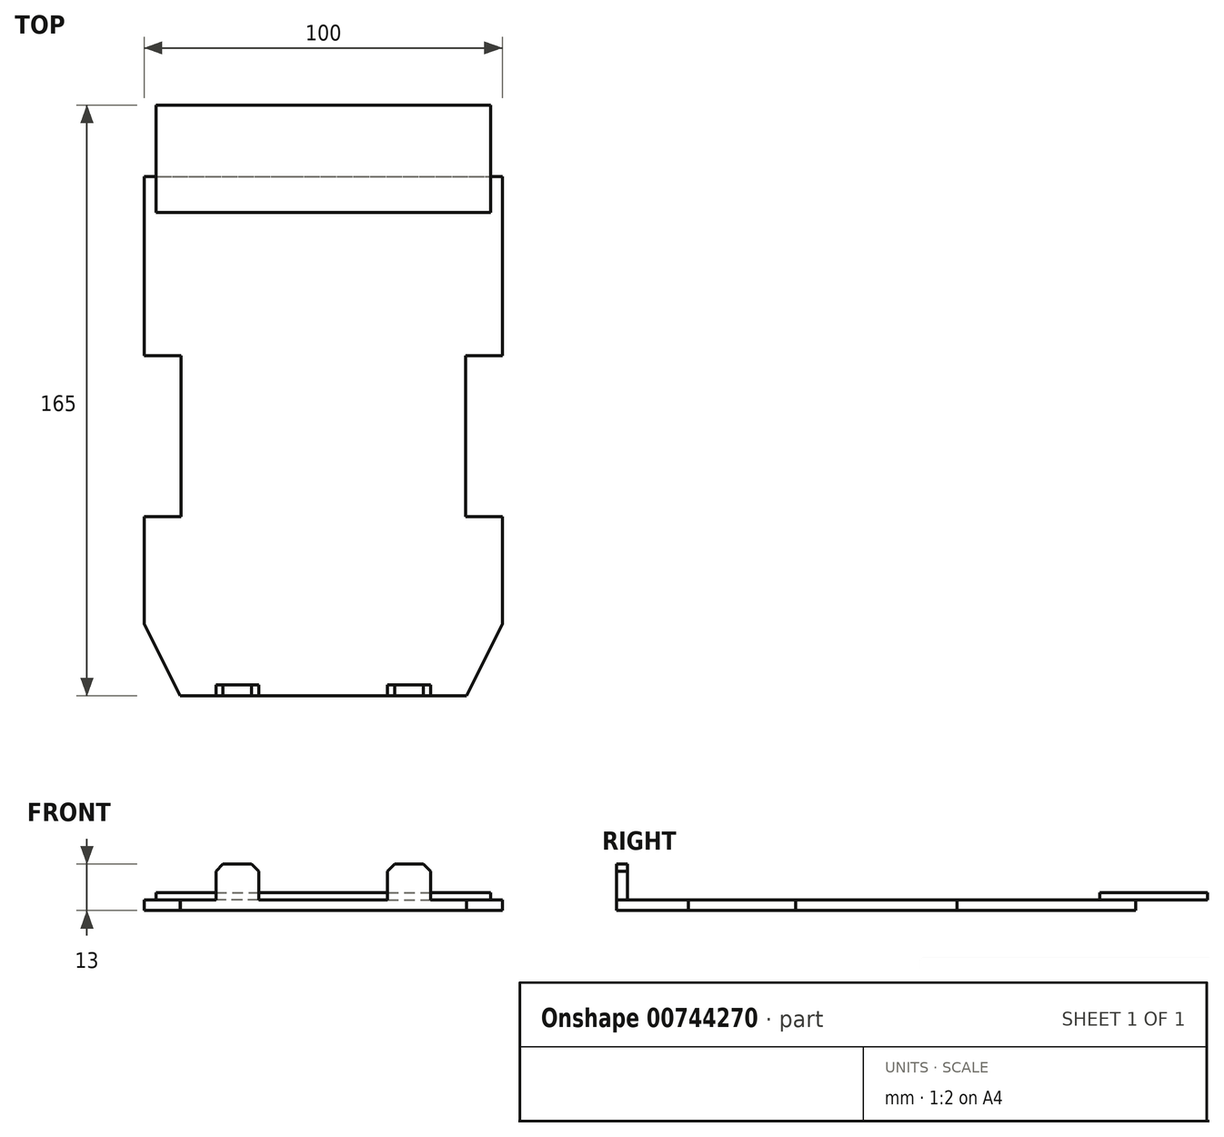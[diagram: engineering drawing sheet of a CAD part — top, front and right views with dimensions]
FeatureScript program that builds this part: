
annotation { "Feature Type Name" : "Feature", "Feature Type Description" : "" }
export const myFeature = defineFeature(function(context is Context, id is Id, definition is map)
    precondition{}
    {
        {
            var Q0;
            Q0=qCreatedBy(makeId("Top.planeOp"),FACE);
            var sketch = newSketch(context, id + "F0", { "sketchPlane" : qUnion([Q0])});
            skLineSegment(sketch, "E0", {"start": v(-30, 56.12) * mm, "end": v(30, 56.12) * mm});
            skLineSegment(sketch, "E1", {"start": v(30, 56.12) * mm, "end": v(50, 41.12) * mm});
            skLineSegment(sketch, "E2", {"start": v(-30, 56.12) * mm, "end": v(-50, 41.12) * mm});
            skLineSegment(sketch, "E3", {"start": v(-50, 41.12) * mm, "end": v(-50, 16.12) * mm});
            skLineSegment(sketch, "E4", {"start": v(-50, 16.12) * mm, "end": v(-42.8, 16.12) * mm});
            skLineSegment(sketch, "E5", {"start": v(-42.8, 16.12) * mm, "end": v(-42.8, -8.88) * mm});
            skLineSegment(sketch, "E6", {"start": v(-42.8, -8.88) * mm, "end": v(-50, -8.88) * mm});
            skLineSegment(sketch, "E7", {"start": v(-50, -8.88) * mm, "end": v(-50, -68.88) * mm});
            skLineSegment(sketch, "E8", {"start": v(-50, -68.88) * mm, "end": v(-39.78, -68.88) * mm});
            skLineSegment(sketch, "E9", {"start": v(-39.78, -68.88) * mm, "end": v(-39.78, -113.88) * mm});
            skLineSegment(sketch, "E10", {"start": v(-39.78, -113.88) * mm, "end": v(-50, -113.88) * mm});
            skLineSegment(sketch, "E11", {"start": v(-50, -113.88) * mm, "end": v(-50, -143.88) * mm});
            skLineSegment(sketch, "E12", {"start": v(-50, -143.88) * mm, "end": v(-40, -163.88) * mm});
            skLineSegment(sketch, "E13", {"start": v(-40, -163.88) * mm, "end": v(40, -163.88) * mm});
            skLineSegment(sketch, "E14.MirrorCS", {"start": v(50, 41.12) * mm, "end": v(50, 16.12) * mm});
            skLineSegment(sketch, "E15.MirrorCS", {"start": v(50, 16.12) * mm, "end": v(42.8, 16.12) * mm});
            skLineSegment(sketch, "E16.MirrorCS", {"start": v(42.8, 16.12) * mm, "end": v(42.8, -8.88) * mm});
            skLineSegment(sketch, "E17.MirrorCS", {"start": v(42.8, -8.88) * mm, "end": v(50, -8.88) * mm});
            skLineSegment(sketch, "E18.MirrorCS", {"start": v(50, -8.88) * mm, "end": v(50, -68.88) * mm});
            skLineSegment(sketch, "E19.MirrorCS", {"start": v(50, -68.88) * mm, "end": v(39.78, -68.88) * mm});
            skLineSegment(sketch, "E20.MirrorCS", {"start": v(39.78, -68.88) * mm, "end": v(39.78, -113.88) * mm});
            skLineSegment(sketch, "E21.MirrorCS", {"start": v(39.78, -113.88) * mm, "end": v(50, -113.88) * mm});
            skLineSegment(sketch, "E22.MirrorCS", {"start": v(50, -113.88) * mm, "end": v(50, -143.88) * mm});
            skLineSegment(sketch, "E23.MirrorCS", {"start": v(50, -143.88) * mm, "end": v(40, -163.88) * mm});
            skLineSegment(sketch, "E24", {"start": v(-50, -18.88) * mm, "end": v(50, -18.88) * mm});
            skSolve(sketch);
        }
        {
            var Q0;
            {var subQ0=sQuery(id+"F0.wireOp",EDGE,"E8");Q0=makeQuery(id+"F0.imprint","IMPRINT",FACE,{"disambiguationData":[TD([[makeQuery(id+"F0.imprint","IMPRINT",EDGE,{"derivedFrom":subQ0}),1.0]])]});}
            extrude(context, id + "F1", {"entities" : qUnion([Q0]), "depth" : 3 * mm, "offsetDistance" : 25 * mm});
        }
        {
            var Q0;
            Q0=makeQuery(id+"F1.opExtrude","CAP_FACE",FACE,{"disambiguationData":[OSD([sQuery(id+"F0.wireOp",EDGE,"E0"),sQuery(id+"F0.wireOp",EDGE,"E1"),sQuery(id+"F0.wireOp",EDGE,"E2"),sQuery(id+"F0.wireOp",EDGE,"E3"),sQuery(id+"F0.wireOp",EDGE,"E4"),sQuery(id+"F0.wireOp",EDGE,"E5"),sQuery(id+"F0.wireOp",EDGE,"E6"),sQuery(id+"F0.wireOp",EDGE,"E7"),sQuery(id+"F0.wireOp",EDGE,"E8"),sQuery(id+"F0.wireOp",EDGE,"E9"),sQuery(id+"F0.wireOp",EDGE,"E10"),sQuery(id+"F0.wireOp",EDGE,"E11"),sQuery(id+"F0.wireOp",EDGE,"E12"),sQuery(id+"F0.wireOp",EDGE,"E13"),sQuery(id+"F0.wireOp",EDGE,"E14.MirrorCS"),sQuery(id+"F0.wireOp",EDGE,"E15.MirrorCS"),sQuery(id+"F0.wireOp",EDGE,"E16.MirrorCS"),sQuery(id+"F0.wireOp",EDGE,"E17.MirrorCS"),sQuery(id+"F0.wireOp",EDGE,"E18.MirrorCS"),sQuery(id+"F0.wireOp",EDGE,"E19.MirrorCS"),sQuery(id+"F0.wireOp",EDGE,"E20.MirrorCS"),sQuery(id+"F0.wireOp",EDGE,"E21.MirrorCS"),sQuery(id+"F0.wireOp",EDGE,"E22.MirrorCS"),sQuery(id+"F0.wireOp",EDGE,"E23.MirrorCS")])],"isStart":false});
            var sketch = newSketch(context, id + "F2", { "sketchPlane" : qUnion([Q0])});
            skLineSegment(sketch, "E25.bottom", {"start": v(-18, -163.88) * mm, "end": v(-30, -163.88) * mm});
            skLineSegment(sketch, "E25.top", {"start": v(-18, -160.88) * mm, "end": v(-30, -160.88) * mm});
            skLineSegment(sketch, "E25.left", {"start": v(-18, -163.88) * mm, "end": v(-18, -160.88) * mm});
            skLineSegment(sketch, "E25.right", {"start": v(-30, -163.88) * mm, "end": v(-30, -160.88) * mm});
            skLineSegment(sketch, "E26.bottom", {"start": v(18, -163.88) * mm, "end": v(30, -163.88) * mm});
            skLineSegment(sketch, "E26.top", {"start": v(18, -160.88) * mm, "end": v(30, -160.88) * mm});
            skLineSegment(sketch, "E26.left", {"start": v(18, -163.88) * mm, "end": v(18, -160.88) * mm});
            skLineSegment(sketch, "E26.right", {"start": v(30, -163.88) * mm, "end": v(30, -160.88) * mm});
            skSolve(sketch);
        }
        {
            var Q0;
            Q0=qSketchRegion(id+"F2",true);
            extrude(context, id + "F3", {"entities" : qUnion([Q0]), "operationType" : NewBodyOperationType.ADD, "depth" : 10 * mm, "offsetDistance" : 25 * mm});
        }
        {
            var Q0;
            Q0=makeQuery(id+"F3.opExtrude","CAP_EDGE",EDGE,{"disambiguationData":[OSD([sQuery(id+"F2.wireOp",EDGE,"8869e0d6-fc5d-49f2-ac7a-9f138a312a912.MirrorCS")])],"isStart":false});
            var Q1;
            Q1=makeQuery(id+"F3.opExtrude","CAP_EDGE",EDGE,{"disambiguationData":[OSD([sQuery(id+"F2.wireOp",EDGE,"8869e0d6-fc5d-49f2-ac7a-9f138a312a913.MirrorCS")])],"isStart":false});
            var Q2;
            Q2=makeQuery(id+"F3.opExtrude","CAP_EDGE",EDGE,{"disambiguationData":[OSD([sQuery(id+"F2.wireOp",EDGE,"bU8oaFip-Qw70-BMbs-t18F-JME3lk5dBetJ.right")])],"isStart":false});
            var Q3;
            Q3=makeQuery(id+"F3.opExtrude","CAP_EDGE",EDGE,{"disambiguationData":[OSD([sQuery(id+"F2.wireOp",EDGE,"bU8oaFip-Qw70-BMbs-t18F-JME3lk5dBetJ.left")])],"isStart":false});
            var Q4;
            Q4=makeQuery(id+"F3.opExtrude","CAP_EDGE",EDGE,{"disambiguationData":[OSD([sQuery(id+"F2.wireOp",EDGE,"E25.left")])],"isStart":false});
            var Q5;
            Q5=makeQuery(id+"F3.opExtrude","CAP_EDGE",EDGE,{"disambiguationData":[OSD([sQuery(id+"F2.wireOp",EDGE,"E25.right")])],"isStart":false});
            var Q6;
            Q6=makeQuery(id+"F3.opExtrude","CAP_EDGE",EDGE,{"disambiguationData":[OSD([sQuery(id+"F2.wireOp",EDGE,"E26.right")])],"isStart":false});
            var Q7;
            Q7=makeQuery(id+"F3.opExtrude","CAP_EDGE",EDGE,{"disambiguationData":[OSD([sQuery(id+"F2.wireOp",EDGE,"E26.left")])],"isStart":false});
            chamfer(context, id + "F4", {"entities" : qUnion([Q0, Q1, Q2, Q3, Q4, Q5, Q6, Q7]), "width" : 2 * mm, "tangentPropagation" : true});
        }
        {
            var Q0;
            Q0=makeQuery(id+"F1.opExtrude","CAP_FACE",FACE,{"disambiguationData":[OSD([sQuery(id+"F0.wireOp",EDGE,"E7"),sQuery(id+"F0.wireOp",EDGE,"E8"),sQuery(id+"F0.wireOp",EDGE,"E9"),sQuery(id+"F0.wireOp",EDGE,"E10"),sQuery(id+"F0.wireOp",EDGE,"E11"),sQuery(id+"F0.wireOp",EDGE,"E12"),sQuery(id+"F0.wireOp",EDGE,"E13"),sQuery(id+"F0.wireOp",EDGE,"E18.MirrorCS"),sQuery(id+"F0.wireOp",EDGE,"E19.MirrorCS"),sQuery(id+"F0.wireOp",EDGE,"E20.MirrorCS"),sQuery(id+"F0.wireOp",EDGE,"E21.MirrorCS"),sQuery(id+"F0.wireOp",EDGE,"E22.MirrorCS"),sQuery(id+"F0.wireOp",EDGE,"E23.MirrorCS"),sQuery(id+"F0.wireOp",EDGE,"E24")])],"isStart":false});
            var sketch = newSketch(context, id + "F5", { "sketchPlane" : qUnion([Q0])});
            skLineSegment(sketch, "E27.bottom", {"start": v(-46.75, -28.88) * mm, "end": v(46.75, -28.88) * mm});
            skLineSegment(sketch, "E27.top", {"start": v(-46.75, 1.12) * mm, "end": v(46.75, 1.12) * mm});
            skLineSegment(sketch, "E27.left", {"start": v(-46.75, -28.88) * mm, "end": v(-46.75, 1.12) * mm});
            skLineSegment(sketch, "E27.right", {"start": v(46.75, -28.88) * mm, "end": v(46.75, 1.12) * mm});
            skSolve(sketch);
        }
        {
            var Q0;
            Q0 = qSketchRegion(id + "F5", true);
            extrude(context, id + "F6", {"entities" : qUnion([Q0]), "operationType" : NewBodyOperationType.ADD, "depth" : 2 * mm, "offsetDistance" : 25 * mm});
        }
    });
